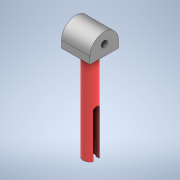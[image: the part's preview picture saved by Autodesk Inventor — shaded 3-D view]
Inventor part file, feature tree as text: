
AUTODESK INVENTOR PART (.ipt)
format: ipt  version: 2022 (Build 260153000, 153)  size: 160,256 bytes
history: native  units: mm
features: extrude x5, sketch x5, fillet x1
ambient origin geometry x8: Origin, YZ Plane, XZ Plane, XY Plane, X Axis, Y Axis, Z Axis, Center Point
bodies: Solid1 (feature_tree)
feature tree (11):
  extrude  "Extrusion1"  Depth=33.0mm TaperAngle=0.0deg
  extrude  "Extrusion2"  Depth=5.0mm
  fillet  "Fillet1"  Radius=5.0mm
  extrude  "Extrusion3"  Depth=5.0mm
  extrude  "Extrusion5"  TaperAngle=0.0deg  [1 undecoded]
  extrude  "Extrusion6"  Depth=5.0mm TaperAngle=0.0deg
  sketch  "Sketch1"  dims[d0=4.8mm d1=33.0mm d2=0.0mm]
  sketch  "Sketch2"  dims[d4=10.0mm d5=5.0mm d6=5.0mm]
  sketch  "Sketch3"  dims[d7=7.5mm d8=0.0mm d9=5.0mm]
  sketch  "Sketch5"  dims[d10=2.2mm d11=0.0mm d12=0.0mm]
  sketch  "Sketch6"  dims[d19=3.0mm d20=5.0mm d21=0.0mm d22=1.0mm d23=8.0mm d24=2.1mm d25=0.0mm d26=0.0mm]
note: 1 required parameter value undecoded (feature->parameter linkage not recoverable at this tier; creation-order binding heuristic only, values carry confidence <= 0.55)
